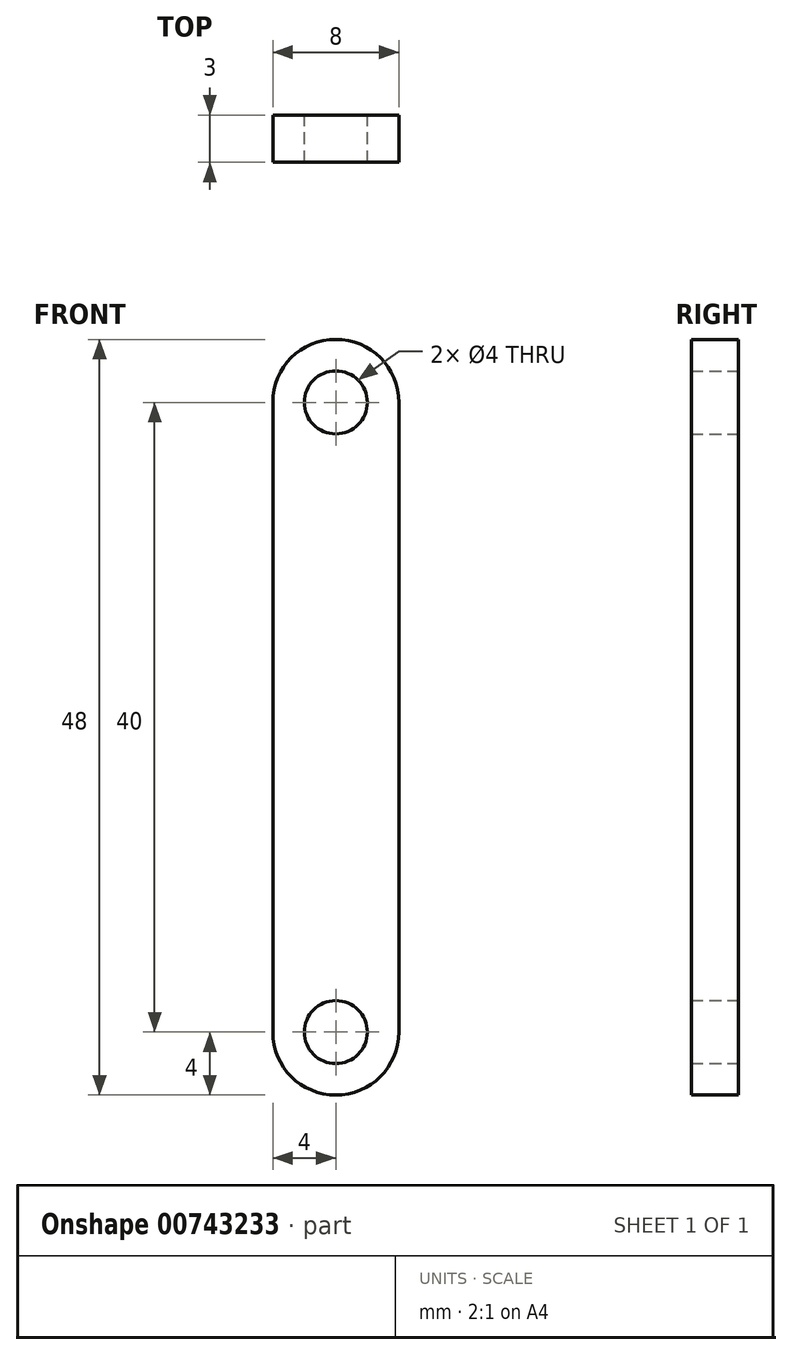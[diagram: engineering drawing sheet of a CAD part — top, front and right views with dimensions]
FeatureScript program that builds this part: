
annotation { "Feature Type Name" : "Feature", "Feature Type Description" : "" }
export const myFeature = defineFeature(function(context is Context, id is Id, definition is map)
    precondition{}
    {
        {
            var Q0;
            Q0=qCreatedBy(makeId("Front.planeOp"),FACE);
            var sketch = newSketch(context, id + "F0", { "sketchPlane" : qUnion([Q0])});
            skLineSegment(sketch, "E0.bottom", {"start": v(4, 20) * mm, "end": v(-4, 20) * mm, "construction": true});
            skLineSegment(sketch, "E0.top", {"start": v(4, -20) * mm, "end": v(-4, -20) * mm, "construction": true});
            skLineSegment(sketch, "E0.left", {"start": v(4, 20) * mm, "end": v(4, -20) * mm});
            skLineSegment(sketch, "E0.right", {"start": v(-4, 20) * mm, "end": v(-4, -20) * mm});
            skPoint(sketch, "E0.middle", {"position": v(0, 0) * mm});
            skArc(sketch, "E1", {"start": v(4, 20) * mm, "mid": v(0, 24) * mm, "end": v(-4, 20) * mm});
            skArc(sketch, "E2", {"start": v(-4, -20) * mm, "mid": v(0, -24) * mm, "end": v(4, -20) * mm});
            skCircle(sketch, "E3", {"center": v(0, 20) * mm, "radius": 2 * mm});
            skCircle(sketch, "E4", {"center": v(0, -20) * mm, "radius": 2 * mm});
            skSolve(sketch);
        }
        {
            var Q0;
            Q0=qSketchRegion(id+"F0",true);
            extrude(context, id + "F1", {"entities" : qUnion([Q0]), "depth" : 3 * mm, "offsetDistance" : 25 * mm});
        }
    });
